# Revit family: GIRA_1209005
name_source: partatom
category: Elektroinstallationen
revit_build: Autodesk Revit 2017 (Build: 20160225_1515(x64)
units: mm (PartAtom-declared; Revit-internal decimal feet)

## family parameters
Basisbauteil = Fläche
Beim Laden mit Abzugskörper schneiden = Nein
Bemaßung runder Anschluss = Durchmesser verwenden
Beschriftungsausrichtung beibehalten = Ja
Gemeinsam genutzt = Nein
Raumberechnungspunkt = Nein
Teiletyp = Normal

## types (1)
- GIRA_1209005
    Abhörsicher = Ja
    Ausführung der Schnittstelle = sonstige
    BIM = https://media.stage.bim.site 005.rfa
    Bedienung Türöffner = Ja
    Beschreibung = Wohnungsstation Video AP 7 Schwarz matt Merkmale:<BR>- Komplett vormontierte Einheit mit einem 17,78 cm (7) großen TFT-Farbdisplay und komfortabler Freisprechfunktion.<BR>- Vollflächige Glasfront mit Touchfunktionalität und taktiler Rückmeldung.<BR>- Direkte Wandmontage oder Wandmontage mit Unterputz-Gerätedose bzw. Hohlwanddose.<BR>- Montage mit Standfuß für Platzierung auf Möbelstücken."
    Bildsystem = PAL
    Freisprechen = Ja
    Funktions-Lampen = Nein
    GTIN = 4010337053408
    HAN = 1209005
    Hersteller = Gira
    Hörgerätekompatibel = Nein
    Internkommunikation = Ja
    Ist System = Nein
    Ist Zubehör = Nein
    Lautstärkeregelung = Ja
    Material = Black Matt
    Mit Touchscreen = Ja
    Mit Türöffnerautomatik = Ja
    Rufabschaltung = Ja
    Rufunterscheidung = Ja
    Schaltfunktionen = Ja
    Typname = Wohnungsstation Video AP 7 Türko Schwarz m
    URL = https://www.gira.de
    Verbindung mit Smartphone möglich = Nein
    Vorgabe-Ansicht = 1219 mm
    Zusatzgerät anreihbar = Ja

## geometry (parser evidence)
native form markers: Sweep x2
no freeform markers — native parametric forms only
